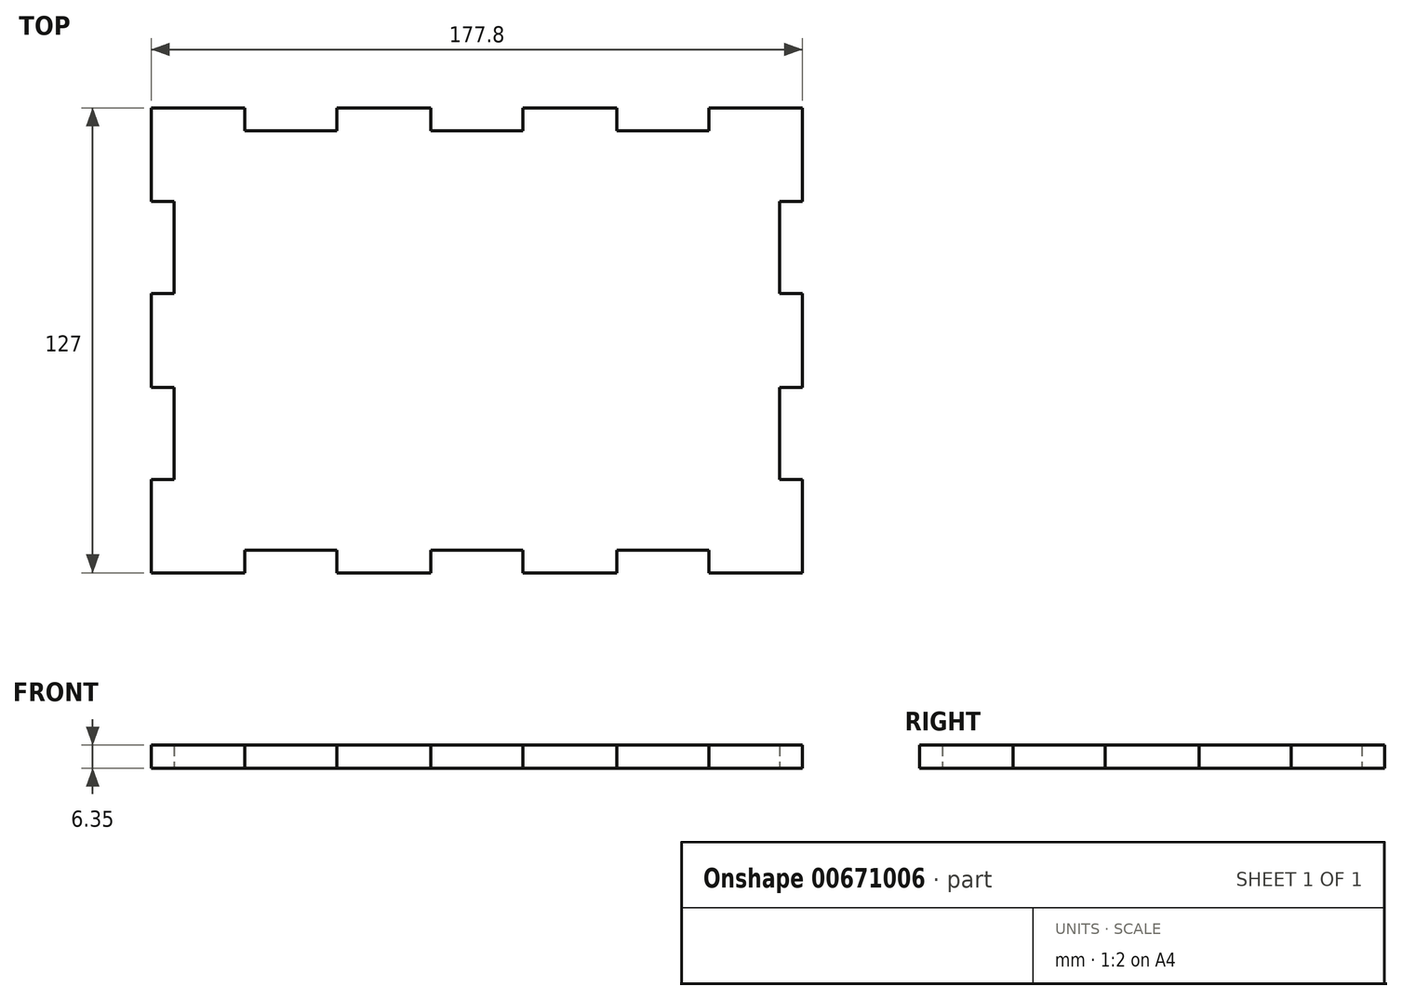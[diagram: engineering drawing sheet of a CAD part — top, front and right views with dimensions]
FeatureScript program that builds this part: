
annotation { "Feature Type Name" : "Feature", "Feature Type Description" : "" }
export const myFeature = defineFeature(function(context is Context, id is Id, definition is map)
    precondition{}
    {
        {
            var Q0;
            Q0=qCreatedBy(makeId("Top.planeOp"),FACE);
            var sketch = newSketch(context, id + "F0", { "sketchPlane" : qUnion([Q0])});
            skLineSegment(sketch, "E0.bottom", {"start": v(0, 0) * mm, "end": v(177.8, 0) * mm});
            skLineSegment(sketch, "E0.top", {"start": v(0, 127) * mm, "end": v(177.8, 127) * mm});
            skLineSegment(sketch, "E0.left", {"start": v(0, 0) * mm, "end": v(0, 127) * mm});
            skLineSegment(sketch, "E0.right", {"start": v(177.8, 0) * mm, "end": v(177.8, 127) * mm});
            skLineSegment(sketch, "E1.bottom", {"start": v(25.49, 0) * mm, "end": v(50.71, 0) * mm});
            skLineSegment(sketch, "E1.top", {"start": v(25.49, 6.26) * mm, "end": v(50.71, 6.26) * mm});
            skLineSegment(sketch, "E1.left", {"start": v(25.49, 0) * mm, "end": v(25.49, 6.26) * mm});
            skLineSegment(sketch, "E1.right", {"start": v(50.71, 0) * mm, "end": v(50.71, 6.26) * mm});
            skPoint(sketch, "E2", {"position": v(38.1, 6.26) * mm});
            skLineSegment(sketch, "E3.bottom", {"start": v(76.29, 0) * mm, "end": v(101.51, 0) * mm});
            skLineSegment(sketch, "E3.top", {"start": v(76.29, 6.26) * mm, "end": v(101.51, 6.26) * mm});
            skLineSegment(sketch, "E3.left", {"start": v(76.29, 0) * mm, "end": v(76.29, 6.26) * mm});
            skLineSegment(sketch, "E3.right", {"start": v(101.51, 0) * mm, "end": v(101.51, 6.26) * mm});
            skPoint(sketch, "E4", {"position": v(88.9, 6.26) * mm});
            skLineSegment(sketch, "E5.bottom", {"start": v(127.09, 0) * mm, "end": v(152.31, 0) * mm});
            skLineSegment(sketch, "E5.top", {"start": v(127.09, 6.26) * mm, "end": v(152.31, 6.26) * mm});
            skLineSegment(sketch, "E5.left", {"start": v(127.09, 0) * mm, "end": v(127.09, 6.26) * mm});
            skLineSegment(sketch, "E5.right", {"start": v(152.31, 0) * mm, "end": v(152.31, 6.26) * mm});
            skPoint(sketch, "E6", {"position": v(139.7, 6.26) * mm});
            skLineSegment(sketch, "E7.bottom", {"start": v(177.8, 25.49) * mm, "end": v(171.54, 25.49) * mm});
            skLineSegment(sketch, "E7.top", {"start": v(177.8, 50.71) * mm, "end": v(171.54, 50.71) * mm});
            skLineSegment(sketch, "E7.left", {"start": v(177.8, 25.49) * mm, "end": v(177.8, 50.71) * mm});
            skLineSegment(sketch, "E7.right", {"start": v(171.54, 25.49) * mm, "end": v(171.54, 50.71) * mm});
            skPoint(sketch, "E8", {"position": v(171.54, 38.1) * mm});
            skLineSegment(sketch, "E9.bottom", {"start": v(177.8, 76.29) * mm, "end": v(171.54, 76.29) * mm});
            skLineSegment(sketch, "E9.top", {"start": v(177.8, 101.51) * mm, "end": v(171.54, 101.51) * mm});
            skLineSegment(sketch, "E9.left", {"start": v(177.8, 76.29) * mm, "end": v(177.8, 101.51) * mm});
            skLineSegment(sketch, "E9.right", {"start": v(171.54, 76.29) * mm, "end": v(171.54, 101.51) * mm});
            skPoint(sketch, "E10", {"position": v(171.54, 88.9) * mm});
            skLineSegment(sketch, "E11", {"start": v(0, 63.5) * mm, "end": v(177.8, 63.5) * mm, "construction": true});
            skLineSegment(sketch, "E12", {"start": v(88.9, 127) * mm, "end": v(88.9, 0) * mm, "construction": true});
            skLineSegment(sketch, "E13.MirrorCS", {"start": v(50.71, 127) * mm, "end": v(50.71, 120.74) * mm});
            skLineSegment(sketch, "E14.MirrorCS", {"start": v(25.49, 120.74) * mm, "end": v(50.71, 120.74) * mm});
            skLineSegment(sketch, "E15.MirrorCS", {"start": v(25.49, 127) * mm, "end": v(50.71, 127) * mm});
            skLineSegment(sketch, "E16.MirrorCS", {"start": v(25.49, 127) * mm, "end": v(25.49, 120.74) * mm});
            skLineSegment(sketch, "E17.MirrorCS", {"start": v(101.51, 127) * mm, "end": v(101.51, 120.74) * mm});
            skLineSegment(sketch, "E18.MirrorCS", {"start": v(76.29, 120.74) * mm, "end": v(101.51, 120.74) * mm});
            skLineSegment(sketch, "E19.MirrorCS", {"start": v(76.29, 127) * mm, "end": v(76.29, 120.74) * mm});
            skLineSegment(sketch, "E20.MirrorCS", {"start": v(76.29, 127) * mm, "end": v(101.51, 127) * mm});
            skLineSegment(sketch, "E21.MirrorCS", {"start": v(127.09, 127) * mm, "end": v(127.09, 120.74) * mm});
            skLineSegment(sketch, "E22.MirrorCS", {"start": v(127.09, 120.74) * mm, "end": v(152.31, 120.74) * mm});
            skLineSegment(sketch, "E23.MirrorCS", {"start": v(127.09, 127) * mm, "end": v(152.31, 127) * mm});
            skLineSegment(sketch, "E24.MirrorCS", {"start": v(152.31, 127) * mm, "end": v(152.31, 120.74) * mm});
            skLineSegment(sketch, "E25.MirrorCS", {"start": v(0, 101.51) * mm, "end": v(6.26, 101.51) * mm});
            skLineSegment(sketch, "E26.MirrorCS", {"start": v(6.26, 76.29) * mm, "end": v(6.26, 101.51) * mm});
            skLineSegment(sketch, "E27.MirrorCS", {"start": v(0, 76.29) * mm, "end": v(6.26, 76.29) * mm});
            skLineSegment(sketch, "E28.MirrorCS", {"start": v(0, 76.29) * mm, "end": v(0, 101.51) * mm});
            skLineSegment(sketch, "E29.MirrorCS", {"start": v(0, 50.71) * mm, "end": v(6.26, 50.71) * mm});
            skLineSegment(sketch, "E30.MirrorCS", {"start": v(6.26, 25.49) * mm, "end": v(6.26, 50.71) * mm});
            skLineSegment(sketch, "E31.MirrorCS", {"start": v(0, 25.49) * mm, "end": v(6.26, 25.49) * mm});
            skLineSegment(sketch, "E32.MirrorCS", {"start": v(0, 25.49) * mm, "end": v(0, 50.71) * mm});
            skSolve(sketch);
        }
        {
            var Q0;
            Q0=makeQuery(id+"F0.imprint","IMPRINT",FACE,{"disambiguationData":[TD([[makeQuery(id+"F0.imprint","IMPRINT",EDGE,{"derivedFrom":sQuery(id+"F0.wireOp",EDGE,"E1.top")}),1.0]])]});
            extrude(context, id + "F1", {"entities" : qUnion([Q0]), "depth" : 6.35 * mm, "offsetDistance" : 25.4 * mm});
        }
    });
